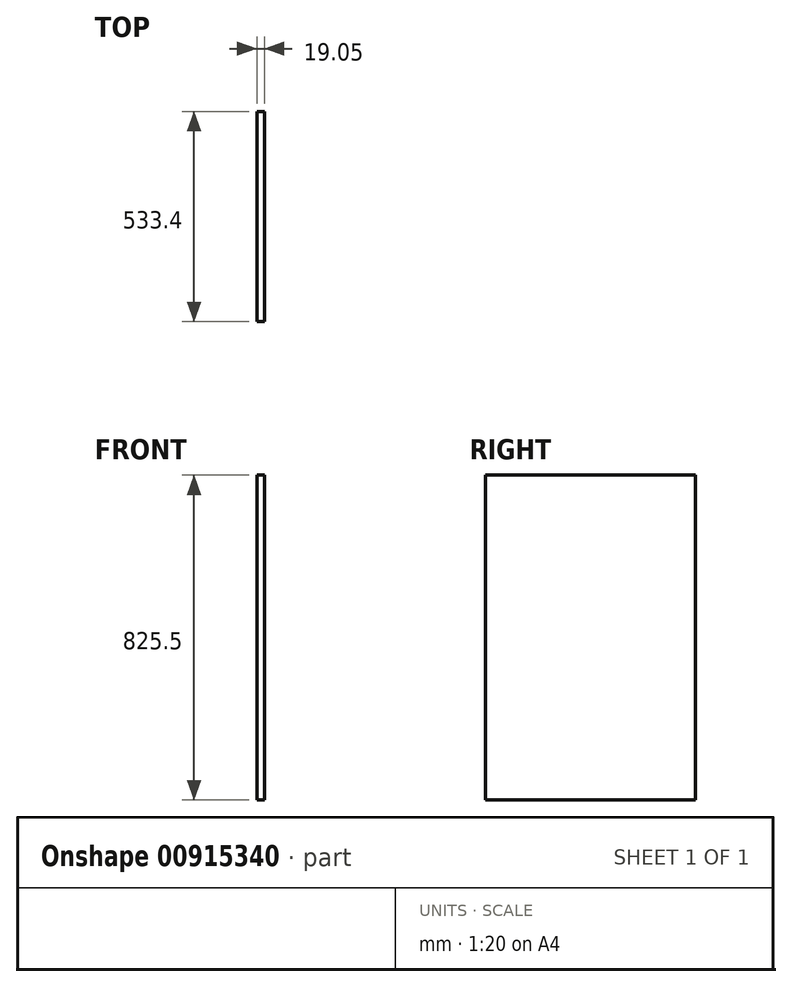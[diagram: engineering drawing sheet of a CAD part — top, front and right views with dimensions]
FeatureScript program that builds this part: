
annotation { "Feature Type Name" : "Feature", "Feature Type Description" : "" }
export const myFeature = defineFeature(function(context is Context, id is Id, definition is map)
    precondition{}
    {
        {
            var Q0;
            Q0=qCreatedBy(makeId("Right.planeOp"),FACE);
            var sketch = newSketch(context, id + "F0", { "sketchPlane" : qUnion([Q0])});
            skLineSegment(sketch, "E0.bottom", {"start": v(0, 0) * mm, "end": v(533.4, 0) * mm});
            skLineSegment(sketch, "E0.top", {"start": v(0, 825.5) * mm, "end": v(533.4, 825.5) * mm});
            skLineSegment(sketch, "E0.left", {"start": v(0, 0) * mm, "end": v(0, 825.5) * mm});
            skLineSegment(sketch, "E0.right", {"start": v(533.4, 0) * mm, "end": v(533.4, 825.5) * mm});
            skSolve(sketch);
        }
        {
            var Q0;
            Q0 = qSketchRegion(id + "F0", true);
            extrude(context, id + "F1", {"entities" : qUnion([Q0]), "depth" : 19.05 * mm, "offsetDistance" : 25.4 * mm});
        }
    });
